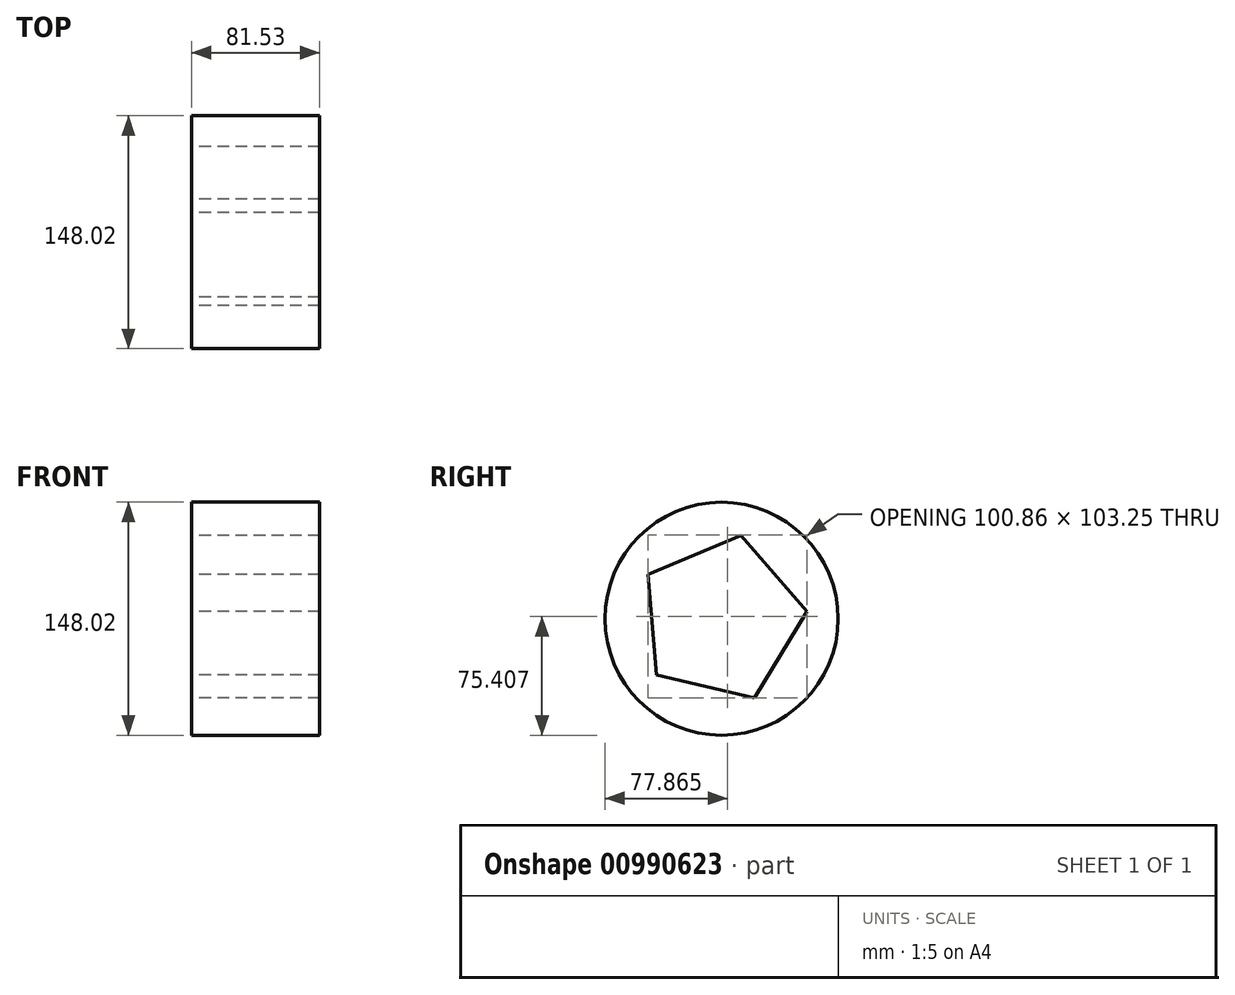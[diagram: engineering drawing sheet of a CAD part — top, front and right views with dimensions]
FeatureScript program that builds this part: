
annotation { "Feature Type Name" : "Feature", "Feature Type Description" : "" }
export const myFeature = defineFeature(function(context is Context, id is Id, definition is map)
    precondition{}
    {
        {
            var Q0;
            Q0=qCreatedBy(makeId("Right.planeOp"),FACE);
            var sketch = newSketch(context, id + "F0", { "sketchPlane" : qUnion([Q0])});
            skCircle(sketch, "E0", {"center": v(0, 0) * mm, "radius": 74 * mm});
            skSolve(sketch);
        }
        {
            var Q0;
            Q0=makeQuery(id+"F0.imprint","IMPRINT",FACE,{"disambiguationData":[TD([[makeQuery(id+"F0.imprint","IMPRINT",EDGE,{"derivedFrom":sQuery(id+"F0.wireOp",EDGE,"E0")}),1.0]])]});
            extrude(context, id + "F1", {"entities" : qUnion([Q0]), "depth" : 81.53 * mm, "offsetDistance" : 25.4 * mm});
        }
        {
            var Q0;
            Q0=makeQuery(id+"F0.imprint","IMPRINT",FACE,{"disambiguationData":[TD([[makeQuery(id+"F0.imprint","IMPRINT",EDGE,{"derivedFrom":sQuery(id+"F0.wireOp",EDGE,"E0")}),1.0]])]});
            var sketch = newSketch(context, id + "F2", { "sketchPlane" : qUnion([Q0])});
            skCircle(sketch, "E1.cCircle", {"center": v(0, 0) * mm, "radius": 44.07 * mm, "construction": true});
            skLineSegment(sketch, "E1.0", {"start": v(12.48, 53.02) * mm, "end": v(54.28, 4.52) * mm});
            skLineSegment(sketch, "E1.1", {"start": v(54.28, 4.52) * mm, "end": v(21.07, -50.23) * mm});
            skLineSegment(sketch, "E1.2", {"start": v(21.07, -50.23) * mm, "end": v(-41.26, -35.56) * mm});
            skLineSegment(sketch, "E1.3", {"start": v(-41.26, -35.56) * mm, "end": v(-46.57, 28.25) * mm});
            skLineSegment(sketch, "E1.4", {"start": v(-46.57, 28.25) * mm, "end": v(12.48, 53.02) * mm});
            skPoint(sketch, "E1.0.midPoint", {"position": v(33.38, 28.77) * mm});
            skSolve(sketch);
        }
        {
            var Q0;
            Q0=makeQuery(id+"F2.imprint","IMPRINT",FACE,{"disambiguationData":[TD([[makeQuery(id+"F2.imprint","IMPRINT",EDGE,{"derivedFrom":sQuery(id+"F2.wireOp",EDGE,"E1.0")}),-1.0]])]});
            extrude(context, id + "F3", {"entities" : qUnion([Q0]), "operationType" : NewBodyOperationType.REMOVE, "depth" : 226.06 * mm, "offsetDistance" : 25.4 * mm});
        }
    });
